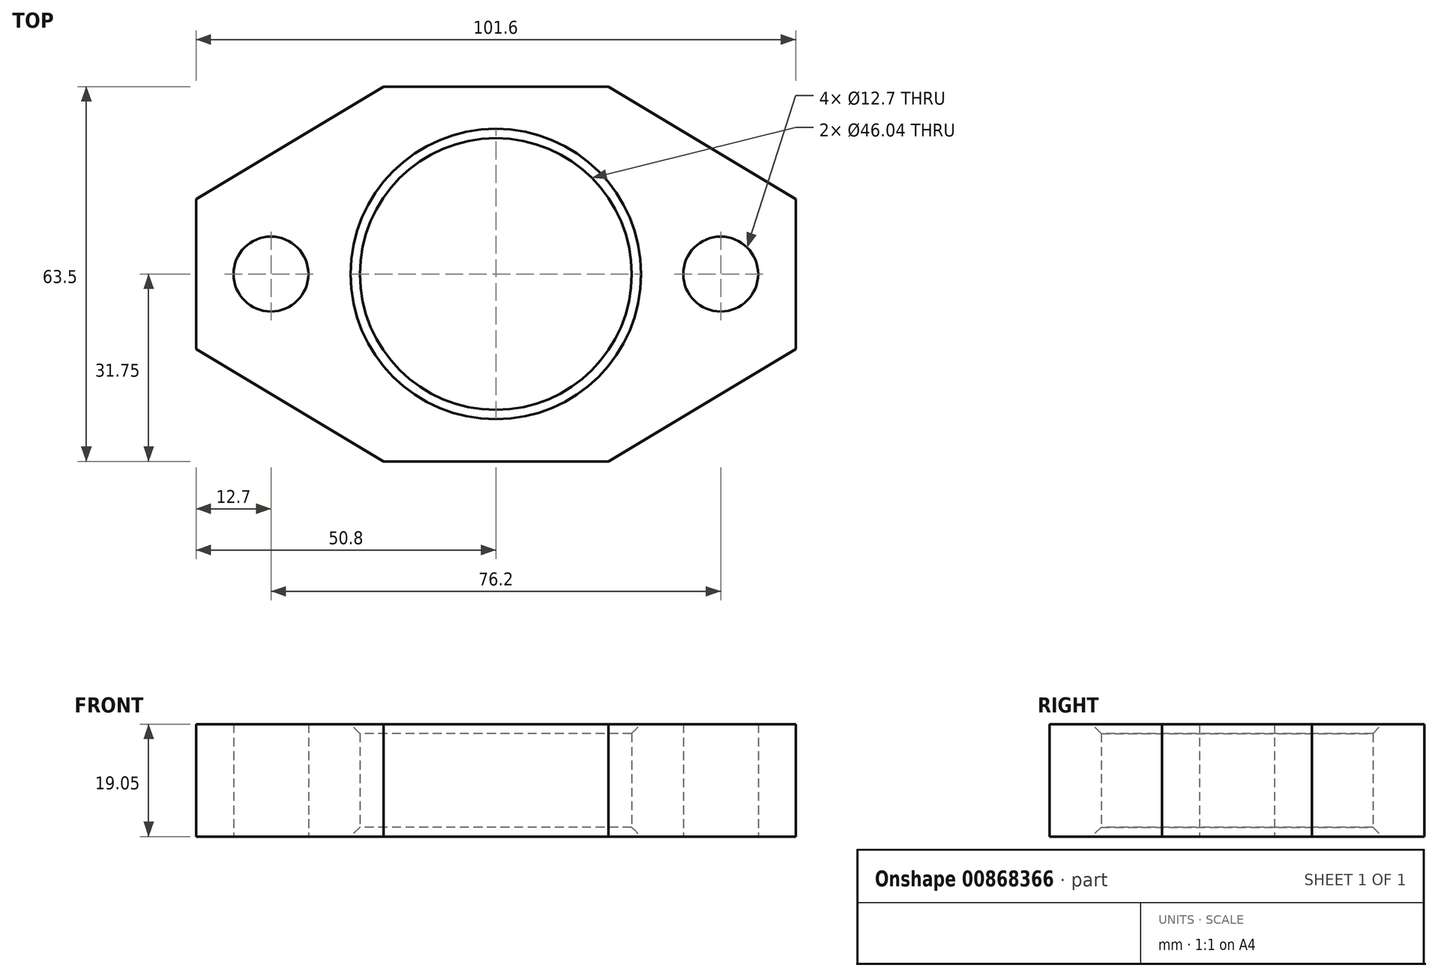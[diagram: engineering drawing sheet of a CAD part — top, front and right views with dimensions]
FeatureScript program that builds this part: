
annotation { "Feature Type Name" : "Feature", "Feature Type Description" : "" }
export const myFeature = defineFeature(function(context is Context, id is Id, definition is map)
    precondition{}
    {
        {
            var Q0;
            Q0=qCreatedBy(makeId("Top.planeOp"),FACE);
            var sketch = newSketch(context, id + "F0", { "sketchPlane" : qUnion([Q0])});
            skLineSegment(sketch, "E0.bottom", {"start": v(19.05, -31.75) * mm, "end": v(-19.05, -31.75) * mm});
            skLineSegment(sketch, "E0.top", {"start": v(19.05, 31.75) * mm, "end": v(-19.05, 31.75) * mm});
            skLineSegment(sketch, "E0.left", {"start": v(50.8, -12.7) * mm, "end": v(50.8, 12.7) * mm});
            skLineSegment(sketch, "E0.right", {"start": v(-50.8, -12.7) * mm, "end": v(-50.8, 12.7) * mm});
            skPoint(sketch, "E0.middle", {"position": v(0, 0) * mm});
            skLineSegment(sketch, "E1", {"start": v(-19.05, 31.75) * mm, "end": v(-50.8, 12.7) * mm});
            skLineSegment(sketch, "E2.MirrorCS", {"start": v(-19.05, -31.75) * mm, "end": v(-50.8, -12.7) * mm});
            skLineSegment(sketch, "E3.MirrorCS", {"start": v(19.05, 31.75) * mm, "end": v(50.8, 12.7) * mm});
            skLineSegment(sketch, "E4.MirrorCS", {"start": v(19.05, -31.75) * mm, "end": v(50.8, -12.7) * mm});
            skCircle(sketch, "E5", {"center": v(0, 0) * mm, "radius": 23.02 * mm});
            skCircle(sketch, "E6", {"center": v(-38.1, 0) * mm, "radius": 6.35 * mm});
            skCircle(sketch, "E7.MirrorC", {"center": v(38.1, 0) * mm, "radius": 6.35 * mm});
            skPoint(sketch, "E8.orphan", {"position": v(50.8, -31.75) * mm});
            skPoint(sketch, "E9.orphan", {"position": v(-50.8, -31.75) * mm});
            skPoint(sketch, "E10.orphan", {"position": v(-50.8, 31.75) * mm});
            skPoint(sketch, "E11.orphan", {"position": v(50.8, 31.75) * mm});
            skSolve(sketch);
        }
        {
            var Q0;
            Q0 = qSketchRegion(id + "F0", true);
            extrude(context, id + "F1", {"entities" : qUnion([Q0]), "depth" : 19.05 * mm, "offsetDistance" : 25.4 * mm});
        }
        {
            var Q0;
            Q0=makeQuery(id+"F1.opExtrude","CAP_EDGE",EDGE,{"disambiguationData":[OSD([sQuery(id+"F0.wireOp",EDGE,"E5")])],"isStart":true});
            var Q1;
            Q1=makeQuery(id+"F1.opExtrude","CAP_EDGE",EDGE,{"disambiguationData":[OSD([sQuery(id+"F0.wireOp",EDGE,"E5")])],"isStart":false});
            chamfer(context, id + "F2", {"entities" : qUnion([Q0, Q1]), "width" : 1.59 * mm, "tangentPropagation" : true});
        }
    });
